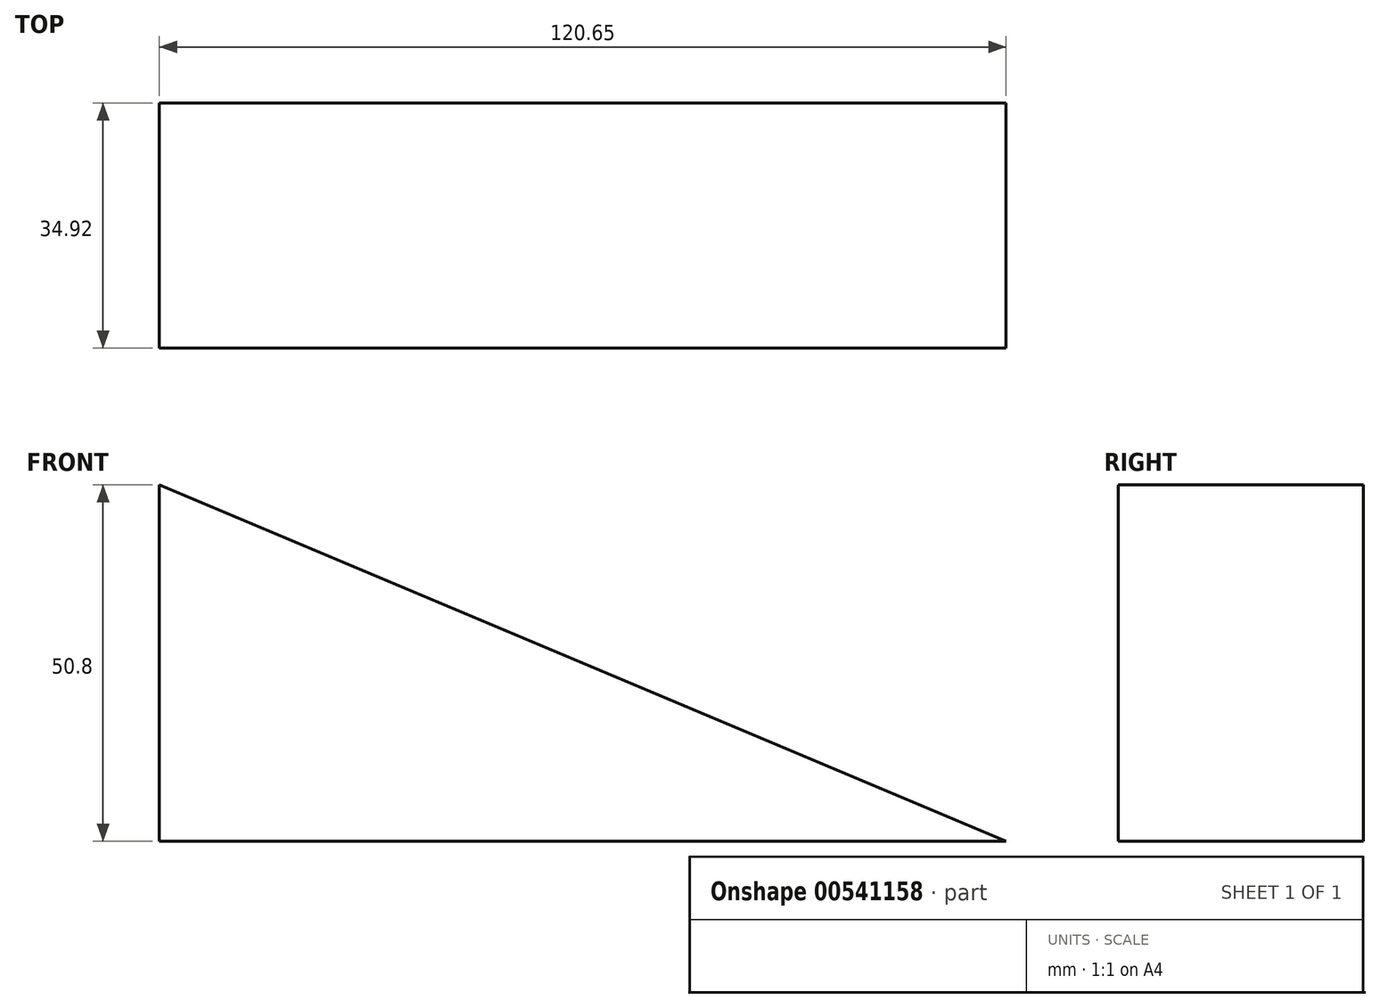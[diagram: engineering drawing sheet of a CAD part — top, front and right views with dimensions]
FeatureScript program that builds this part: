
annotation { "Feature Type Name" : "Feature", "Feature Type Description" : "" }
export const myFeature = defineFeature(function(context is Context, id is Id, definition is map)
    precondition{}
    {
        {
            var Q0;
            Q0=qCreatedBy(makeId("Front.planeOp"),FACE);
            var sketch = newSketch(context, id + "F0", { "sketchPlane" : qUnion([Q0])});
            skLineSegment(sketch, "E0", {"start": v(0, 0) * mm, "end": v(0, 50.8) * mm});
            skLineSegment(sketch, "E1", {"start": v(0, 0) * mm, "end": v(120.65, 0) * mm});
            skLineSegment(sketch, "E2", {"start": v(0, 50.8) * mm, "end": v(120.65, 0) * mm});
            skSolve(sketch);
        }
        {
            var Q0;
            Q0 = qSketchRegion(id + "F0", true);
            extrude(context, id + "F1", {"entities" : qUnion([Q0]), "depth" : 34.92 * mm, "offsetDistance" : 25.4 * mm});
        }
    });
